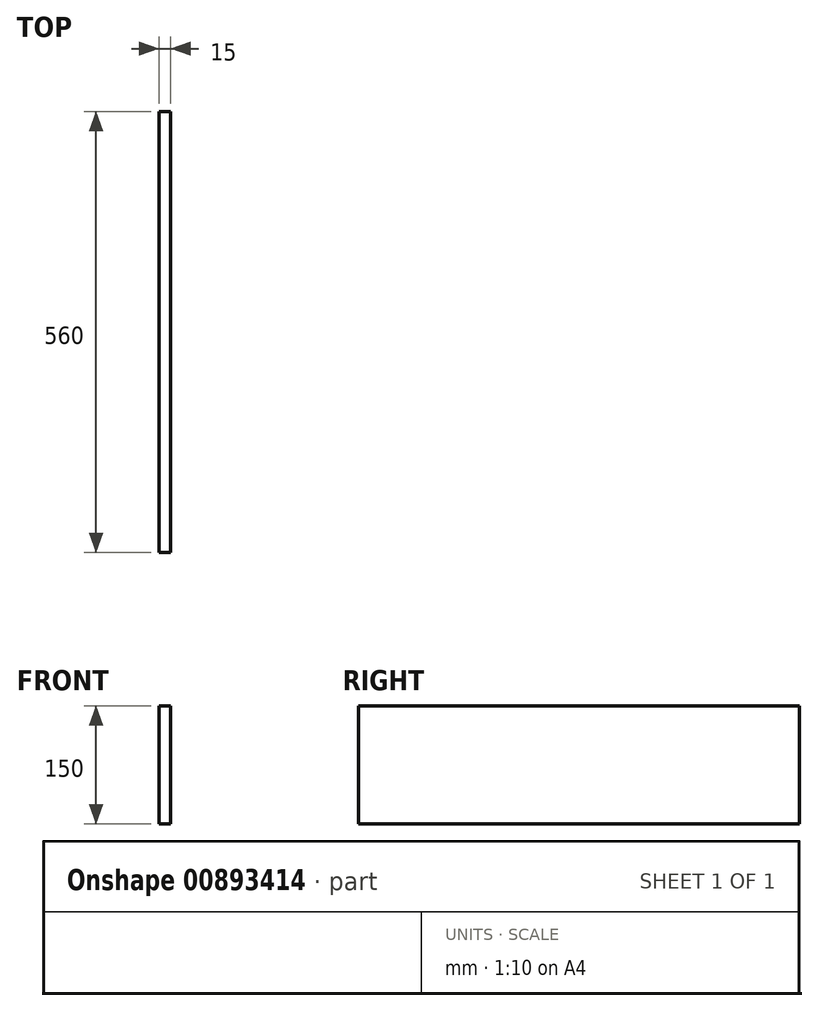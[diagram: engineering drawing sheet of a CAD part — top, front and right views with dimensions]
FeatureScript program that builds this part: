
annotation { "Feature Type Name" : "Feature", "Feature Type Description" : "" }
export const myFeature = defineFeature(function(context is Context, id is Id, definition is map)
    precondition{}
    {
        {
            var Q0;
            Q0=qCreatedBy(makeId("Right.planeOp"),FACE);
            var sketch = newSketch(context, id + "F0", { "sketchPlane" : qUnion([Q0])});
            skLineSegment(sketch, "E0.bottom", {"start": v(0, 0) * mm, "end": v(560, 0) * mm});
            skLineSegment(sketch, "E0.top", {"start": v(0, 150) * mm, "end": v(560, 150) * mm});
            skLineSegment(sketch, "E0.left", {"start": v(0, 0) * mm, "end": v(0, 150) * mm});
            skLineSegment(sketch, "E0.right", {"start": v(560, 0) * mm, "end": v(560, 150) * mm});
            skSolve(sketch);
        }
        {
            var Q0;
            Q0=makeQuery(id+"F0.imprint","IMPRINT",FACE,{"disambiguationData":[TD([[makeQuery(id+"F0.imprint","IMPRINT",EDGE,{"derivedFrom":sQuery(id+"F0.wireOp",EDGE,"E0.bottom")}),1.0]])]});
            extrude(context, id + "F1", {"entities" : qUnion([Q0]), "depth" : 15 * mm, "offsetDistance" : 25 * mm});
        }
    });
